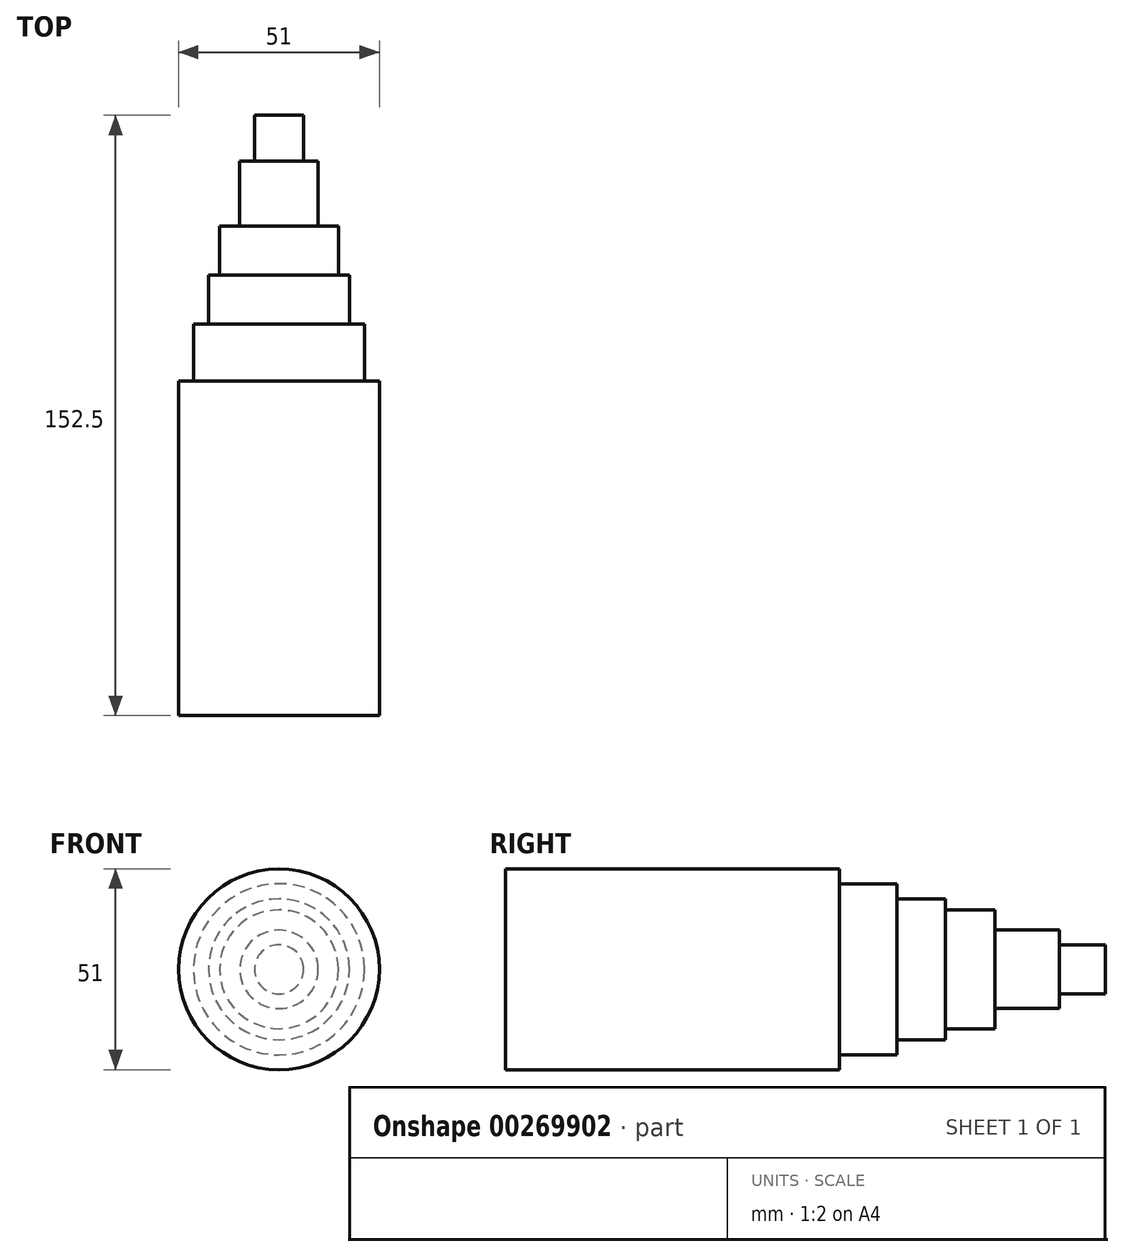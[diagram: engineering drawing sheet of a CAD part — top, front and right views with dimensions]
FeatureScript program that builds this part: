
annotation { "Feature Type Name" : "Feature", "Feature Type Description" : "" }
export const myFeature = defineFeature(function(context is Context, id is Id, definition is map)
    precondition{}
    {
        {
            var Q0;
            Q0=qCreatedBy(makeId("Front.planeOp"),FACE);
            var sketch = newSketch(context, id + "F0", { "sketchPlane" : qUnion([Q0])});
            skCircle(sketch, "E0", {"center": v(0, 0) * mm, "radius": 25.5 * mm});
            skSolve(sketch);
        }
        {
            var Q0;
            Q0=makeQuery(id+"F0.imprint","IMPRINT",FACE,{"disambiguationData":[TD([[makeQuery(id+"F0.imprint","IMPRINT",EDGE,{"derivedFrom":sQuery(id+"F0.wireOp",EDGE,"E0")}),1.0]])]});
            extrude(context, id + "F1", {"entities" : qUnion([Q0]), "oppositeDirection" : true, "depth" : 84.92 * mm});
        }
        {
            var Q0;
            Q0=makeQuery(id+"F1.opExtrude","CAP_FACE",FACE,{"disambiguationData":[OSD([sQuery(id+"F0.wireOp",EDGE,"E0")])],"isStart":false});
            var sketch = newSketch(context, id + "F2", { "sketchPlane" : qUnion([Q0])});
            skCircle(sketch, "E1", {"center": v(0, 0) * mm, "radius": 21.74 * mm});
            skSolve(sketch);
        }
        {
            var Q0;
            Q0=makeQuery(id+"F2.imprint","IMPRINT",FACE,{"disambiguationData":[TD([[makeQuery(id+"F2.imprint","IMPRINT",EDGE,{"derivedFrom":sQuery(id+"F2.wireOp",EDGE,"E1")}),1.0]])]});
            extrude(context, id + "F3", {"entities" : qUnion([Q0]), "operationType" : NewBodyOperationType.ADD, "depth" : 14.52 * mm});
        }
        {
            var Q0;
            Q0=makeQuery(id+"F3.opExtrude","CAP_FACE",FACE,{"disambiguationData":[OSD([sQuery(id+"F2.wireOp",EDGE,"E1")])],"isStart":false});
            var sketch = newSketch(context, id + "F4", { "sketchPlane" : qUnion([Q0])});
            skCircle(sketch, "E2", {"center": v(0, 0) * mm, "radius": 17.9 * mm});
            skSolve(sketch);
        }
        {
            var Q0;
            Q0=makeQuery(id+"F4.imprint","IMPRINT",FACE,{"disambiguationData":[TD([[makeQuery(id+"F4.imprint","IMPRINT",EDGE,{"derivedFrom":sQuery(id+"F4.wireOp",EDGE,"E2")}),1.0]])]});
            extrude(context, id + "F5", {"entities" : qUnion([Q0]), "operationType" : NewBodyOperationType.ADD, "depth" : 12.4 * mm});
        }
        {
            var Q0;
            Q0=makeQuery(id+"F5.opExtrude","CAP_FACE",FACE,{"disambiguationData":[OSD([sQuery(id+"F4.wireOp",EDGE,"E2")])],"isStart":false});
            var sketch = newSketch(context, id + "F6", { "sketchPlane" : qUnion([Q0])});
            skCircle(sketch, "E3", {"center": v(0, 0) * mm, "radius": 15.1 * mm});
            skSolve(sketch);
        }
        {
            var Q0;
            Q0=makeQuery(id+"F6.imprint","IMPRINT",FACE,{"disambiguationData":[TD([[makeQuery(id+"F6.imprint","IMPRINT",EDGE,{"derivedFrom":sQuery(id+"F6.wireOp",EDGE,"E3")}),1.0]])]});
            extrude(context, id + "F7", {"entities" : qUnion([Q0]), "operationType" : NewBodyOperationType.ADD, "depth" : 12.5 * mm});
        }
        {
            var Q0;
            Q0=makeQuery(id+"F7.opExtrude","CAP_FACE",FACE,{"disambiguationData":[OSD([sQuery(id+"F6.wireOp",EDGE,"E3")])],"isStart":false});
            var sketch = newSketch(context, id + "F8", { "sketchPlane" : qUnion([Q0])});
            skCircle(sketch, "E4", {"center": v(0, 0) * mm, "radius": 9.96 * mm});
            skSolve(sketch);
        }
        {
            var Q0;
            Q0=makeQuery(id+"F8.imprint","IMPRINT",FACE,{"disambiguationData":[TD([[makeQuery(id+"F8.imprint","IMPRINT",EDGE,{"derivedFrom":sQuery(id+"F8.wireOp",EDGE,"E4")}),1.0]])]});
            extrude(context, id + "F9", {"entities" : qUnion([Q0]), "operationType" : NewBodyOperationType.ADD, "depth" : 16.46 * mm});
        }
        {
            var Q0;
            Q0=makeQuery(id+"F9.opExtrude","CAP_FACE",FACE,{"disambiguationData":[OSD([sQuery(id+"F8.wireOp",EDGE,"E4")])],"isStart":false});
            var sketch = newSketch(context, id + "F10", { "sketchPlane" : qUnion([Q0])});
            skCircle(sketch, "E5", {"center": v(0, 0) * mm, "radius": 6.23 * mm});
            skSolve(sketch);
        }
        {
            var Q0;
            Q0 = qSketchRegion(id + "F10", true);
            extrude(context, id + "F11", {"entities" : qUnion([Q0]), "operationType" : NewBodyOperationType.ADD, "depth" : 11.7 * mm});
        }
    });
